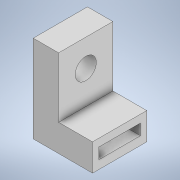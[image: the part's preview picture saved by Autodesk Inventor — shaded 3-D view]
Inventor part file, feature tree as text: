
AUTODESK INVENTOR PART (.ipt)
format: ipt  version: 2020 (Build 240168000, 168)  size: 125,952 bytes
history: native  units: mm
features: extrude x2, sketch x2
ambient origin geometry x8: Origin, YZ Plane, XZ Plane, XY Plane, X Axis, Y Axis, Z Axis, Center Point
bodies: Solid1 (feature_tree)
feature tree (4):
  extrude  "Extrusion1"  Depth=16.0mm
  extrude  "Extrusion2"  Depth=1.875mm
  sketch  "Sketch1"  dims[d0=25.75mm d1=16.0mm]
  sketch  "Sketch2"  dims[d2=2.5mm d4=1.875mm d5=1.875mm d6=3.25mm d7=6.25mm d8=7.5mm d9=0.0mm d10=8.0mm d11=10.0mm d12=0.0mm d13=0.5mm d14=0.872665mm]
